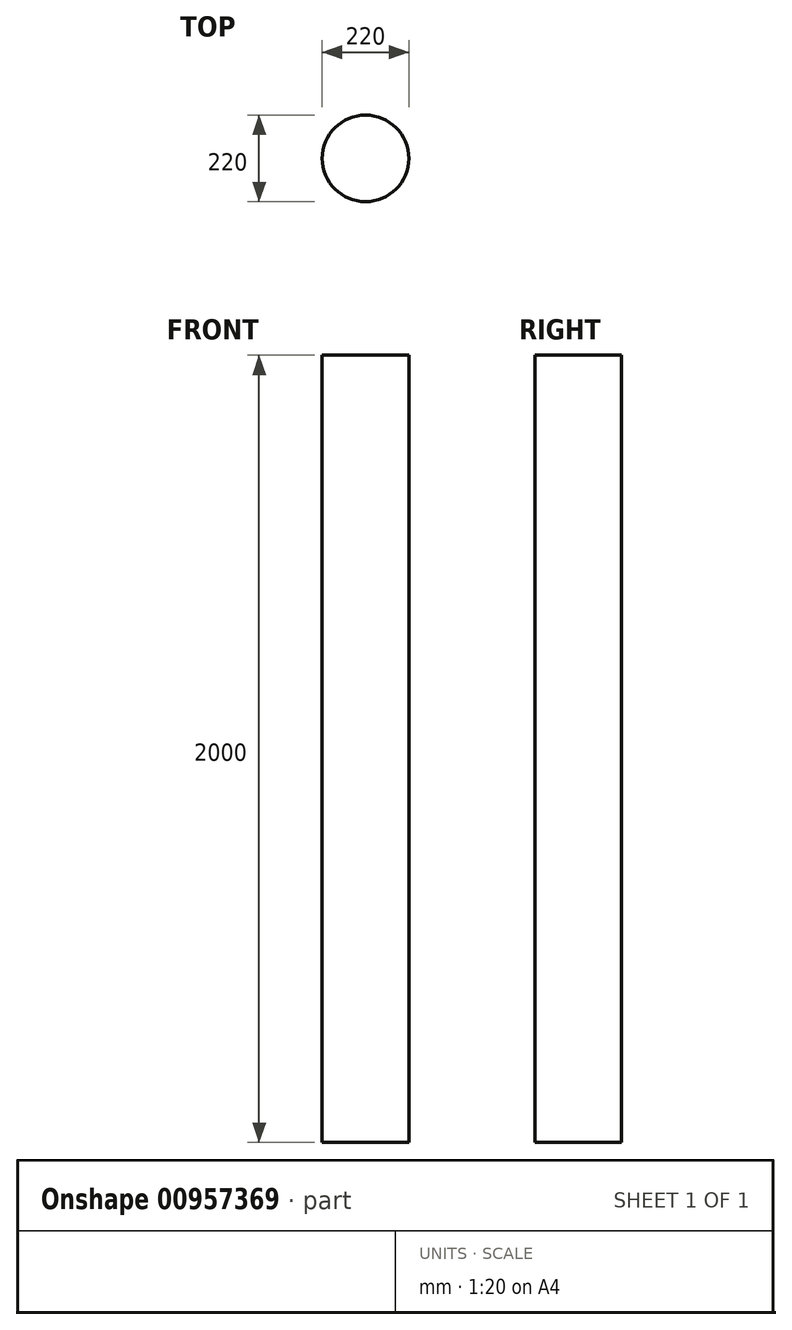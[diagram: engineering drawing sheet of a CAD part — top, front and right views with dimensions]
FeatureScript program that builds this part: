
annotation { "Feature Type Name" : "Feature", "Feature Type Description" : "" }
export const myFeature = defineFeature(function(context is Context, id is Id, definition is map)
    precondition{}
    {
        {
            var Q0;
            Q0=qCreatedBy(makeId("Top.planeOp"),FACE);
            var sketch = newSketch(context, id + "F0", { "sketchPlane" : qUnion([Q0])});
            skCircle(sketch, "E0", {"center": v(0, 0) * mm, "radius": 110 * mm});
            skSolve(sketch);
        }
        {
            var Q0;
            Q0=makeQuery(id+"F0.imprint","IMPRINT",FACE,{"disambiguationData":[TD([[makeQuery(id+"F0.imprint","IMPRINT",EDGE,{"derivedFrom":sQuery(id+"F0.wireOp",EDGE,"E0")}),1.0]])]});
            extrude(context, id + "F1", {"entities" : qUnion([Q0]), "depth" : 2000 * mm, "offsetDistance" : 25 * mm});
        }
    });
